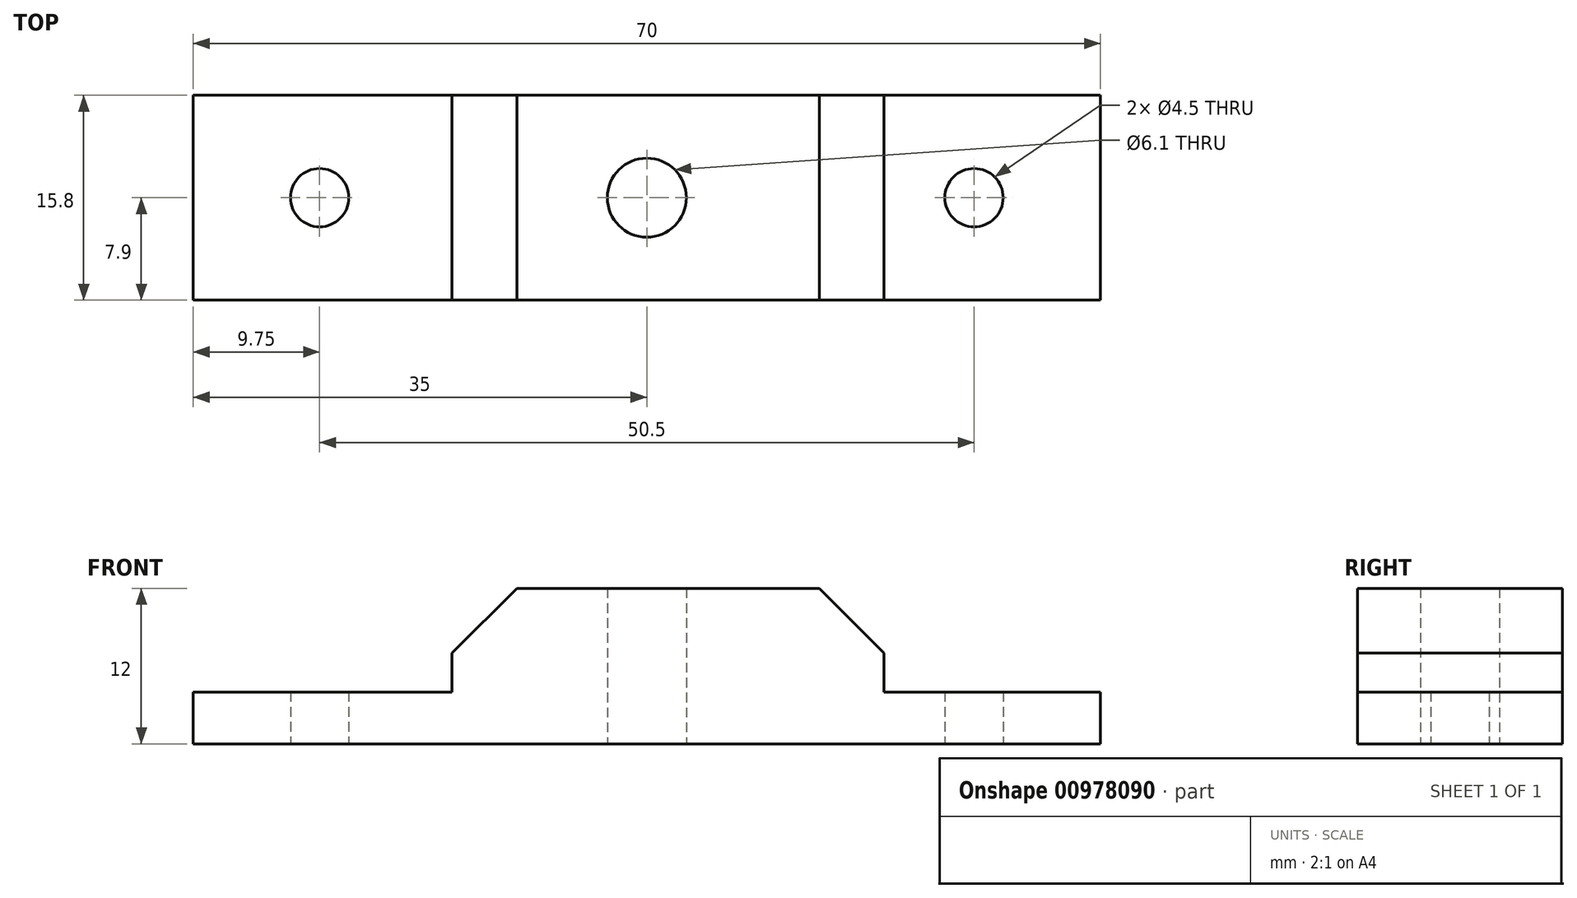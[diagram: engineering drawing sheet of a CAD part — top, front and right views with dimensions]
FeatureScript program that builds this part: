
annotation { "Feature Type Name" : "Feature", "Feature Type Description" : "" }
export const myFeature = defineFeature(function(context is Context, id is Id, definition is map)
    precondition{}
    {
        {
            var Q0;
            Q0=qCreatedBy(makeId("Top.planeOp"),FACE);
            var sketch = newSketch(context, id + "F0", { "sketchPlane" : qUnion([Q0])});
            skLineSegment(sketch, "E0.bottom", {"start": v(-35, 0) * mm, "end": v(35, 0) * mm});
            skLineSegment(sketch, "E0.top", {"start": v(-35, -15.8) * mm, "end": v(35, -15.8) * mm});
            skLineSegment(sketch, "E0.left", {"start": v(-35, 0) * mm, "end": v(-35, -15.8) * mm});
            skLineSegment(sketch, "E0.right", {"start": v(35, 0) * mm, "end": v(35, -15.8) * mm});
            skCircle(sketch, "E1", {"center": v(-25.25, -7.9) * mm, "radius": 2.25 * mm});
            skPoint(sketch, "E1.centerSnap0", {"position": v(-35, -7.9) * mm});
            skCircle(sketch, "E2", {"center": v(25.25, -7.9) * mm, "radius": 2.25 * mm});
            skPoint(sketch, "E2.centerSnap0", {"position": v(35, -7.9) * mm});
            skCircle(sketch, "E3", {"center": v(0, -7.9) * mm, "radius": 3.05 * mm});
            skLineSegment(sketch, "E4.bottom", {"start": v(-15.03, 0) * mm, "end": v(18.31, 0) * mm});
            skLineSegment(sketch, "E4.top", {"start": v(-15.03, -15.8) * mm, "end": v(18.31, -15.8) * mm});
            skLineSegment(sketch, "E4.left", {"start": v(-15.03, 0) * mm, "end": v(-15.03, -15.8) * mm});
            skLineSegment(sketch, "E4.right", {"start": v(18.31, 0) * mm, "end": v(18.31, -15.8) * mm});
            skSolve(sketch);
        }
        {
            var Q0;
            Q0=makeQuery(id+"F0.imprint","IMPRINT",FACE,{"disambiguationData":[TD([[makeQuery(id+"F0.imprint","IMPRINT",EDGE,{"derivedFrom":sQuery(id+"F0.wireOp",EDGE,"E0.bottom")}),-1.0]])]});
            var Q1;
            Q1=makeQuery(id+"F0.imprint","IMPRINT",FACE,{"disambiguationData":[TD([[makeQuery(id+"F0.imprint","IMPRINT",EDGE,{"derivedFrom":sQuery(id+"F0.wireOp",EDGE,"E3")}),-1.0]])]});
            extrude(context, id + "F1", {"entities" : qUnion([Q0, Q1]), "depth" : 4 * mm, "offsetDistance" : 25 * mm});
        }
        {
            var Q0;
            Q0=makeQuery(id+"F0.imprint","IMPRINT",FACE,{"disambiguationData":[TD([[makeQuery(id+"F0.imprint","IMPRINT",EDGE,{"derivedFrom":sQuery(id+"F0.wireOp",EDGE,"E3")}),-1.0]])]});
            extrude(context, id + "F2", {"entities" : qUnion([Q0]), "operationType" : NewBodyOperationType.ADD, "depth" : 12 * mm, "offsetDistance" : 25 * mm});
        }
        {
            var Q0;
            Q0=makeQuery(id+"F2.opExtrude","CAP_EDGE",EDGE,{"disambiguationData":[OSD([sQuery(id+"F0.wireOp",EDGE,"E4.left")])],"isStart":false});
            var Q1;
            Q1=makeQuery(id+"F2.opExtrude","CAP_EDGE",EDGE,{"disambiguationData":[OSD([sQuery(id+"F0.wireOp",EDGE,"E4.right")])],"isStart":false});
            chamfer(context, id + "F3", {"entities" : qUnion([Q0, Q1]), "width" : 5 * mm, "tangentPropagation" : true});
        }
    });
